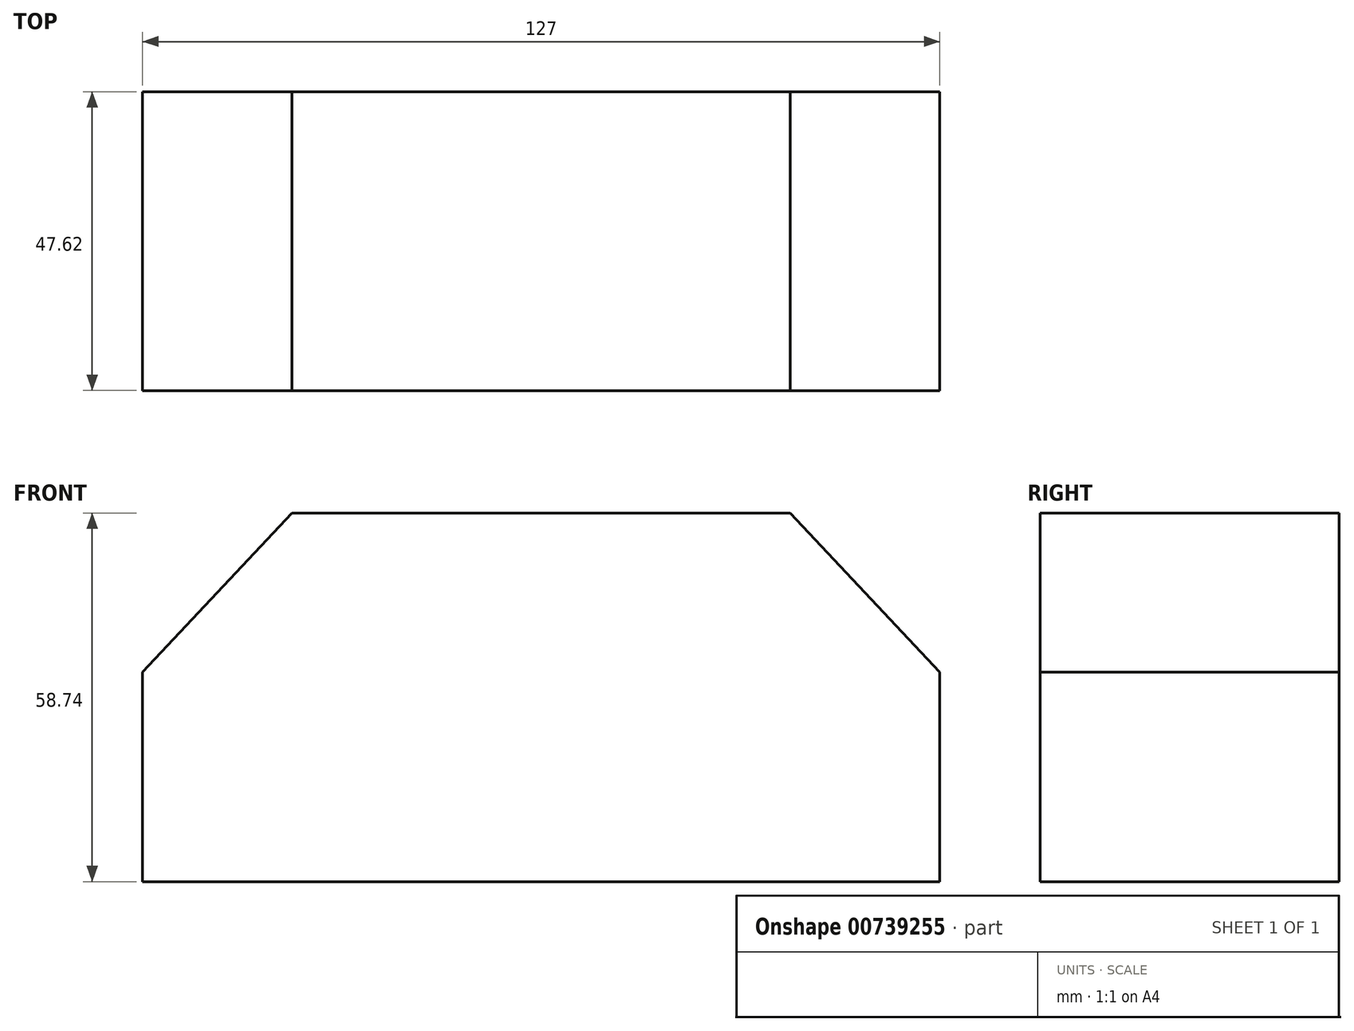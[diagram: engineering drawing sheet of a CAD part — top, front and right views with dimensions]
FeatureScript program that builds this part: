
annotation { "Feature Type Name" : "Feature", "Feature Type Description" : "" }
export const myFeature = defineFeature(function(context is Context, id is Id, definition is map)
    precondition{}
    {
        {
            var Q0;
            Q0=qCreatedBy(makeId("Front.planeOp"),FACE);
            var sketch = newSketch(context, id + "F0", { "sketchPlane" : qUnion([Q0])});
            skLineSegment(sketch, "E0", {"start": v(-86.04, -24.73) * mm, "end": v(40.96, -24.73) * mm});
            skLineSegment(sketch, "E1", {"start": v(-86.04, -24.73) * mm, "end": v(-86.04, 8.62) * mm});
            skLineSegment(sketch, "E2", {"start": v(40.96, 8.62) * mm, "end": v(17.15, 34.01) * mm});
            skLineSegment(sketch, "E3", {"start": v(-86.04, 8.62) * mm, "end": v(-62.23, 34.01) * mm});
            skLineSegment(sketch, "E4", {"start": v(-62.23, 34.01) * mm, "end": v(17.15, 34.01) * mm});
            skLineSegment(sketch, "E5", {"start": v(40.96, 8.62) * mm, "end": v(40.96, -24.73) * mm});
            skSolve(sketch);
        }
        {
            var Q0;
            Q0=makeQuery(id+"F0.imprint","IMPRINT",FACE,{"disambiguationData":[TD([[makeQuery(id+"F0.imprint","IMPRINT",EDGE,{"derivedFrom":sQuery(id+"F0.wireOp",EDGE,"E0")}),1.0]])]});
            extrude(context, id + "F1", {"entities" : qUnion([Q0]), "depth" : 47.62 * mm, "offsetDistance" : 25.4 * mm});
        }
    });
